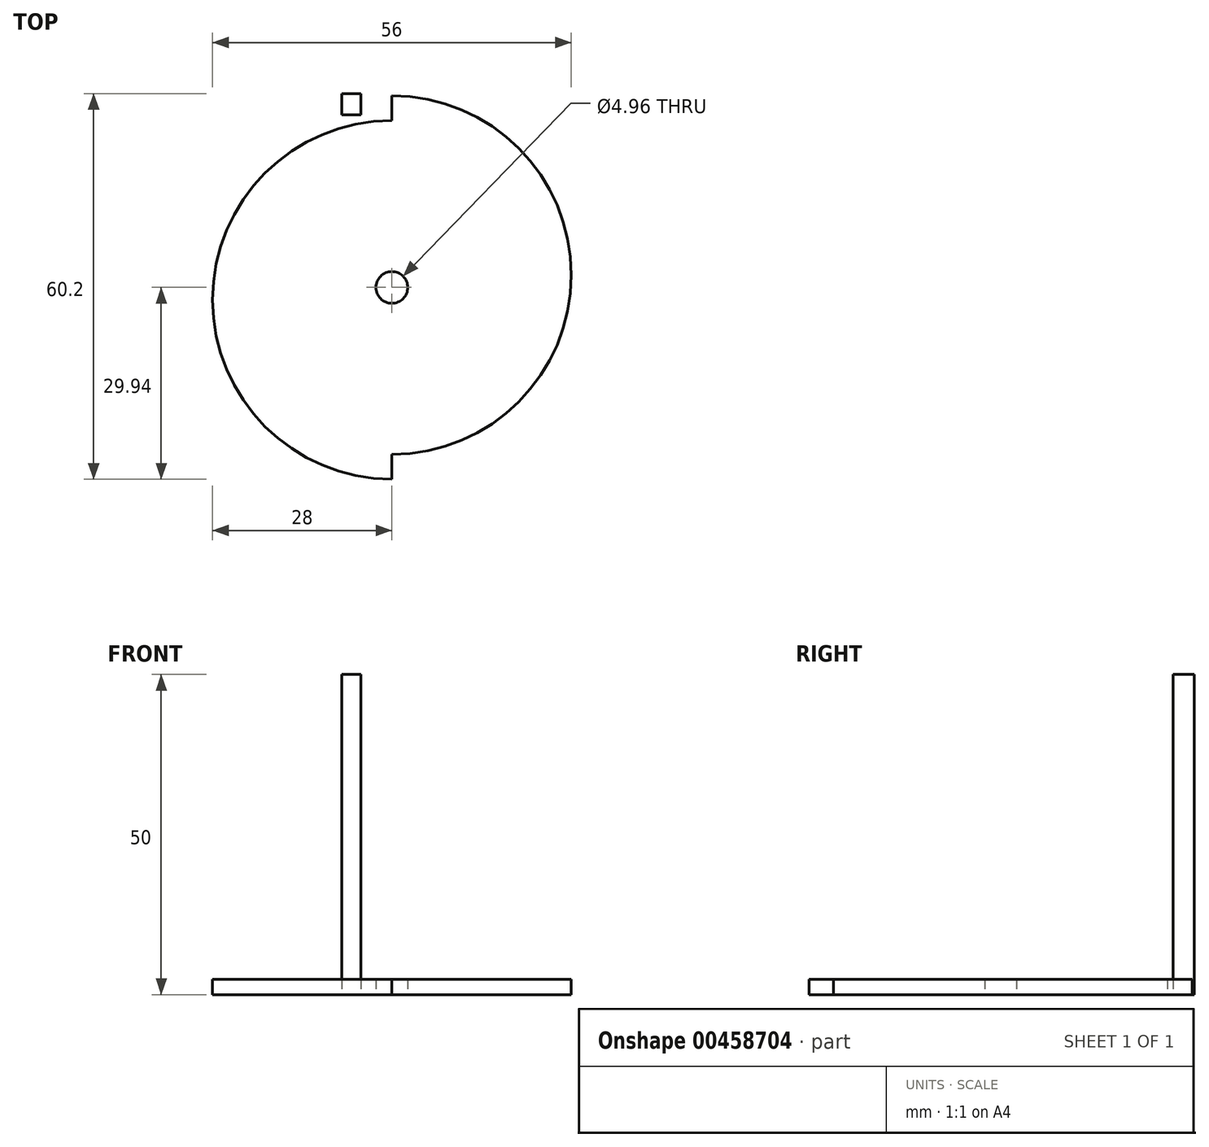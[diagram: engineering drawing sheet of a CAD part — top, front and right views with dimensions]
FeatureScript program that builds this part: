
annotation { "Feature Type Name" : "Feature", "Feature Type Description" : "" }
export const myFeature = defineFeature(function(context is Context, id is Id, definition is map)
    precondition{}
    {
        {
            var Q0;
            Q0=qCreatedBy(makeId("Top.planeOp"),FACE);
            var sketch = newSketch(context, id + "F0", { "sketchPlane" : qUnion([Q0])});
            skCircle(sketch, "E0", {"center": v(0, 0) * mm, "radius": 26.06 * mm});
            skArc(sketch, "E1", {"start": v(0, 26.06) * mm, "mid": v(-28, -1.94) * mm, "end": v(0, -29.94) * mm});
            skLineSegment(sketch, "E2", {"start": v(0, -29.94) * mm, "end": v(0, -26.06) * mm});
            skLineSegment(sketch, "E3.1.0", {"start": v(0, 29.94) * mm, "end": v(0, 26.06) * mm});
            skArc(sketch, "E3.1.1", {"start": v(0, -26.06) * mm, "mid": v(28, 1.94) * mm, "end": v(0, 29.94) * mm});
            skCircle(sketch, "E4", {"center": v(0, 0) * mm, "radius": 2.48 * mm});
            skLineSegment(sketch, "E5.bottom", {"start": v(-7.85, 30.26) * mm, "end": v(-4.85, 30.26) * mm});
            skLineSegment(sketch, "E5.top", {"start": v(-7.85, 26.94) * mm, "end": v(-4.85, 26.94) * mm});
            skLineSegment(sketch, "E5.left", {"start": v(-7.85, 30.26) * mm, "end": v(-7.85, 26.94) * mm});
            skLineSegment(sketch, "E5.right", {"start": v(-4.85, 30.26) * mm, "end": v(-4.85, 26.94) * mm});
            skSolve(sketch);
        }
        {
            var Q0;
            Q0=makeQuery(id+"F0.imprint","IMPRINT",FACE,{"disambiguationData":[TD([[makeQuery(id+"F0.imprint","IMPRINT",EDGE,{"derivedFrom":sQuery(id+"F0.wireOp",EDGE,"E4")}),-1.0]])]});
            var Q1;
            {var subQ0=sQuery(id+"F0.wireOp",EDGE,"E1");Q1=makeQuery(id+"F0.imprint","IMPRINT",FACE,{"disambiguationData":[TD([[makeQuery(id+"F0.imprint","IMPRINT",EDGE,{"derivedFrom":subQ0}),1.0]])]});}
            var Q2;
            {var subQ2=sQuery(id+"F0.wireOp",EDGE,"E3.1.1");Q2=makeQuery(id+"F0.imprint","IMPRINT",FACE,{"disambiguationData":[TD([[makeQuery(id+"F0.imprint","IMPRINT",EDGE,{"derivedFrom":subQ2}),1.0]])]});}
            extrude(context, id + "F1", {"entities" : qUnion([Q0, Q1, Q2]), "depth" : 2.38 * mm, "offsetDistance" : 25 * mm});
        }
        {
            var Q0;
            Q0=makeQuery(id+"F0.imprint","IMPRINT",FACE,{"disambiguationData":[TD([[makeQuery(id+"F0.imprint","IMPRINT",EDGE,{"derivedFrom":sQuery(id+"F0.wireOp",EDGE,"E5.bottom")}),-1.0]])]});
            extrude(context, id + "F2", {"entities" : qUnion([Q0]), "depth" : 50 * mm, "offsetDistance" : 25 * mm});
        }
    });
